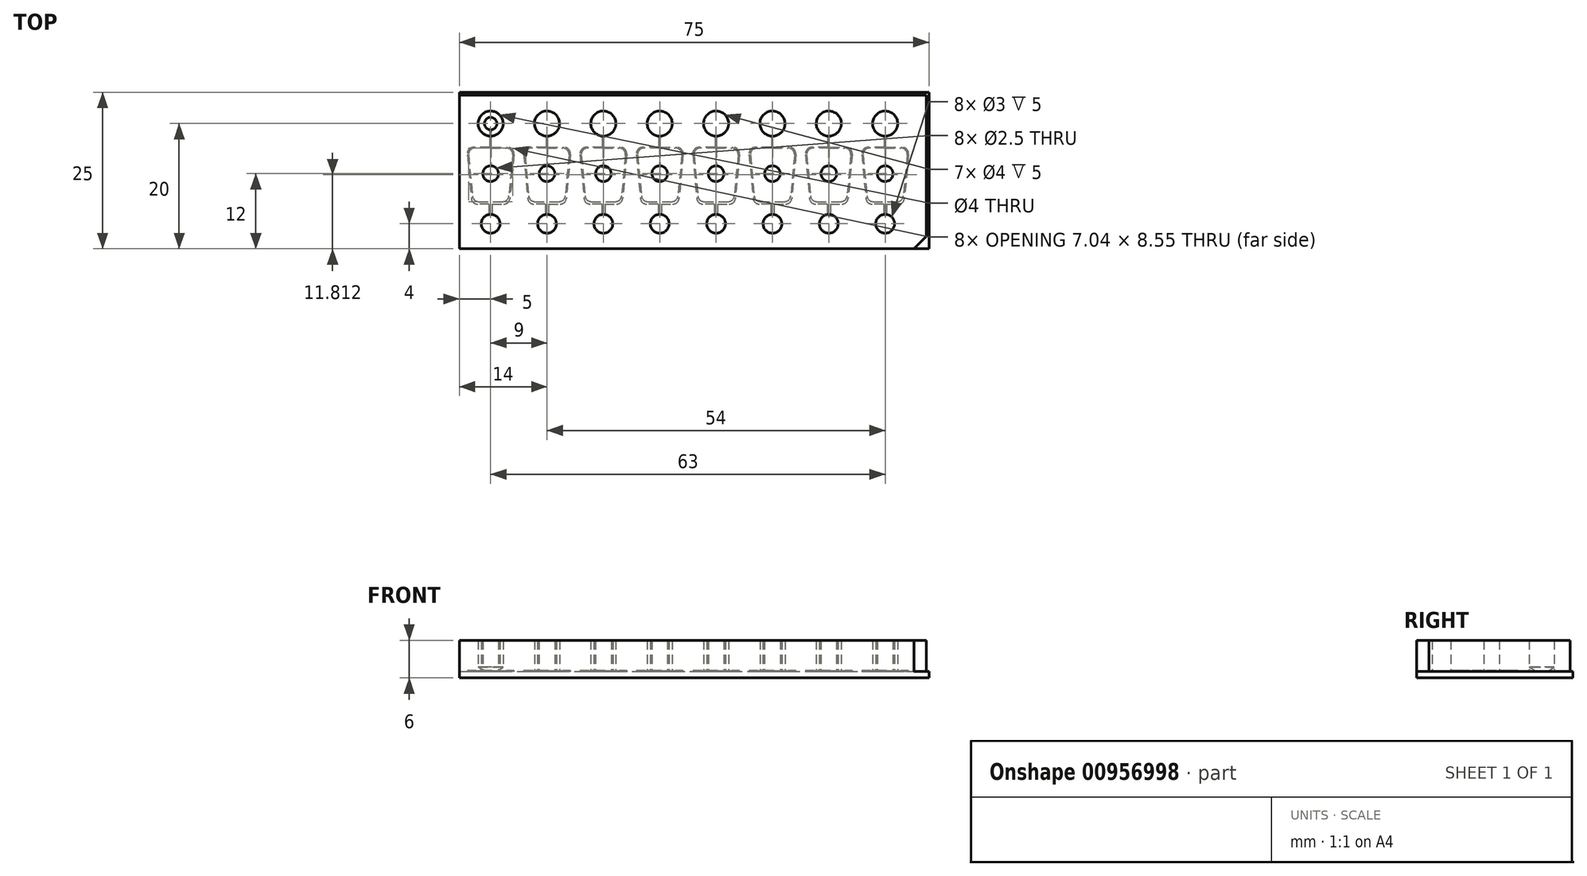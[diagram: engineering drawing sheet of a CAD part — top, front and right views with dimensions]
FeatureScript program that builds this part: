
annotation { "Feature Type Name" : "Feature", "Feature Type Description" : "" }
export const myFeature = defineFeature(function(context is Context, id is Id, definition is map)
    precondition{}
    {
        {
            assignVariable(context, id + "F0", {"name" : "offset_x_ports", "anyValue" : 5});
        }
        {
            var Q0;
            Q0=qCreatedBy(makeId("Top.planeOp"),FACE);
            var sketch = newSketch(context, id + "F1", { "sketchPlane" : qUnion([Q0])});
            skLineSegment(sketch, "E0.bottom", {"start": v(0, 0) * mm, "end": v(74.58, 0) * mm});
            skLineSegment(sketch, "E0.top", {"start": v(0, 24.53) * mm, "end": v(74.58, 24.53) * mm});
            skLineSegment(sketch, "E0.left", {"start": v(0, 0) * mm, "end": v(0, 24.53) * mm});
            skLineSegment(sketch, "E0.right", {"start": v(74.58, 0) * mm, "end": v(74.58, 24.53) * mm});
            skSolve(sketch);
        }
        {
            var Q0;
            Q0 = qSketchRegion(id + "F1", true);
            extrude(context, id + "F2", {"entities" : qUnion([Q0]), "depth" : 5 * mm, "offsetDistance" : 25 * mm});
        }
        {
            var Q0;
            Q0=qCreatedBy(makeId("Top.planeOp"),FACE);
            var sketch = newSketch(context, id + "F3", { "sketchPlane" : qUnion([Q0])});
            skCircle(sketch, "E1", {"center": v(5, 4) * mm, "radius": 1.5 * mm});
            skCircle(sketch, "E2", {"center": v(5, 20) * mm, "radius": 2 * mm});
            skCircle(sketch, "E3", {"center": v(5, 12) * mm, "radius": 1.25 * mm});
            skCircle(sketch, "E4.1.0.0", {"center": v(14, 4) * mm, "radius": 1.5 * mm});
            skCircle(sketch, "E4.1.0.1", {"center": v(14, 12) * mm, "radius": 1.25 * mm});
            skCircle(sketch, "E4.1.0.2", {"center": v(14, 20) * mm, "radius": 2 * mm});
            skCircle(sketch, "E4.2.0.0", {"center": v(23, 4) * mm, "radius": 1.5 * mm});
            skCircle(sketch, "E4.2.0.1", {"center": v(23, 12) * mm, "radius": 1.25 * mm});
            skCircle(sketch, "E4.2.0.2", {"center": v(23, 20) * mm, "radius": 2 * mm});
            skCircle(sketch, "E4.3.0.0", {"center": v(32, 4) * mm, "radius": 1.5 * mm});
            skCircle(sketch, "E4.3.0.1", {"center": v(32, 12) * mm, "radius": 1.25 * mm});
            skCircle(sketch, "E4.3.0.2", {"center": v(32, 20) * mm, "radius": 2 * mm});
            skCircle(sketch, "E4.4.0.0", {"center": v(41, 4) * mm, "radius": 1.5 * mm});
            skCircle(sketch, "E4.4.0.1", {"center": v(41, 12) * mm, "radius": 1.25 * mm});
            skCircle(sketch, "E4.4.0.2", {"center": v(41, 20) * mm, "radius": 2 * mm});
            skCircle(sketch, "E4.5.0.0", {"center": v(50, 4) * mm, "radius": 1.5 * mm});
            skCircle(sketch, "E4.5.0.1", {"center": v(50, 12) * mm, "radius": 1.25 * mm});
            skCircle(sketch, "E4.5.0.2", {"center": v(50, 20) * mm, "radius": 2 * mm});
            skCircle(sketch, "E4.6.0.0", {"center": v(59, 4) * mm, "radius": 1.5 * mm});
            skCircle(sketch, "E4.6.0.1", {"center": v(59, 12) * mm, "radius": 1.25 * mm});
            skCircle(sketch, "E4.6.0.2", {"center": v(59, 20) * mm, "radius": 2 * mm});
            skCircle(sketch, "E4.7.0.0", {"center": v(68, 4) * mm, "radius": 1.5 * mm});
            skCircle(sketch, "E4.7.0.1", {"center": v(68, 12) * mm, "radius": 1.25 * mm});
            skCircle(sketch, "E4.7.0.2", {"center": v(68, 20) * mm, "radius": 2 * mm});
            skLineSegment(sketch, "E4.direction1", {"start": v(5, 4) * mm, "end": v(14, 4) * mm, "construction": true});
            skSolve(sketch);
        }
        {
            var Q0;
            Q0 = qSketchRegion(id + "F3", true);
            var Q1;
            Q1=makeQuery(id+"F2.opExtrude","CAP_FACE",FACE,{"disambiguationData":[OSD([sQuery(id+"F1.wireOp",EDGE,"E0.bottom"),sQuery(id+"F1.wireOp",EDGE,"E0.top"),sQuery(id+"F1.wireOp",EDGE,"E0.left"),sQuery(id+"F1.wireOp",EDGE,"E0.right")])],"isStart":false});
            extrude(context, id + "F4", {"entities" : qUnion([Q0]), "operationType" : NewBodyOperationType.REMOVE, "endBound" : BoundingType.UP_TO_SURFACE, "depth" : 25 * mm, "endBoundEntityFace" : qUnion([Q1]), "offsetDistance" : 25 * mm});
        }
        {
            var Q0;
            Q0=makeQuery(id+"F2.opExtrude","SWEPT_EDGE",EDGE,{"disambiguationData":[OSD([sQuery(id+"F1.wireOp",EDGE,"E0.bottom"),sQuery(id+"F1.wireOp",EDGE,"E0.right")])]});
            chamfer(context, id + "F5", {"entities" : qUnion([Q0]), "width" : 2 * mm, "tangentPropagation" : true});
        }
        {
            var Q0;
            Q0=qCreatedBy(makeId("Top.planeOp"),FACE);
            var sketch = newSketch(context, id + "F6", { "sketchPlane" : qUnion([Q0])});
            skLineSegment(sketch, "E5.bottom", {"start": v(0, 0) * mm, "end": v(75, 0) * mm});
            skLineSegment(sketch, "E5.top", {"start": v(0, 25) * mm, "end": v(75, 25) * mm});
            skLineSegment(sketch, "E5.left", {"start": v(0, 0) * mm, "end": v(0, 25) * mm});
            skLineSegment(sketch, "E5.right", {"start": v(75, 0) * mm, "end": v(75, 25) * mm});
            skSolve(sketch);
        }
        {
            var Q0;
            Q0 = qSketchRegion(id + "F6", true);
            extrude(context, id + "F7", {"entities" : qUnion([Q0]), "oppositeDirection" : true, "depth" : 1 * mm, "offsetDistance" : 25 * mm});
        }
        {
            var Q0;
            Q0=qCreatedBy(makeId("Top.planeOp"),FACE);
            var sketch = newSketch(context, id + "F8", { "sketchPlane" : qUnion([Q0])});
            skPoint(sketch, "E6", {"position": v(5, 4) * mm});
            skLineSegment(sketch, "E7", {"start": v(5, 4) * mm, "end": v(5, 28.43) * mm});
            skSolve(sketch);
        }
        {
            var Q0;
            Q0=qCreatedBy(makeId("Right.planeOp"),FACE);
            cPlane(context, id + "F9", {"entities" : qUnion([Q0]), "cplaneType" : CPlaneType.OFFSET, "offset" : (getVariable(context, 'offset_x_ports')) * mm, "width" : 150 * mm, "height" : 150 * mm});
        }
        {
            var Q0;
            Q0=qCreatedBy(id+"F9.planeOp",FACE);
            var sketch = newSketch(context, id + "F10", { "sketchPlane" : qUnion([Q0])});
            skLineSegment(sketch, "E8", {"start": v(22, 4.38) * mm, "end": v(18, 4.38) * mm});
            skPoint(sketch, "E9", {"position": v(20, 4.38) * mm});
            skLineSegment(sketch, "E10", {"start": v(20, 4.38) * mm, "end": v(20, 0) * mm});
            skLineSegment(sketch, "E11", {"start": v(20, 0) * mm, "end": v(20, -2.07) * mm});
            skLineSegment(sketch, "E12", {"start": v(13.25, 0.89) * mm, "end": v(10.75, 0.89) * mm});
            skSolve(sketch);
        }
        {
            var Q0;
            Q0=qCreatedBy(id+"F9.planeOp",FACE);
            var sketch = newSketch(context, id + "F11", { "sketchPlane" : qUnion([Q0])});
            skLineSegment(sketch, "E13", {"start": v(22, 0) * mm, "end": v(22, 0.72) * mm});
            skLineSegment(sketch, "E14", {"start": v(22, 0.72) * mm, "end": v(21, 0) * mm});
            skLineSegment(sketch, "E15", {"start": v(21, 0) * mm, "end": v(22, 0) * mm});
            skSolve(sketch);
        }
        {
            var Q0;
            Q0 = qSketchRegion(id + "F11", true);
            var Q1;
            Q1=sQuery(id+"F10.wireOp",EDGE,"E10");
            revolve(context, id + "F12", {"operationType" : NewBodyOperationType.ADD, "surfaceOperationType" : NewSurfaceOperationType.NEW, "entities" : qUnion([Q0]), "axis" : qUnion([Q1]), "revolveType" : RevolveType.FULL});
        }
        {
            var Q0;
            Q0=qCreatedBy(makeId("Top.planeOp"),FACE);
            var sketch = newSketch(context, id + "F13", { "sketchPlane" : qUnion([Q0])});
            skLineSegment(sketch, "E16", {"start": v(5.03, 16.09) * mm, "end": v(7.52, 16.09) * mm});
            skLineSegment(sketch, "E17", {"start": v(5.2, 16.19) * mm, "end": v(7.73, 16.19) * mm});
            skLineSegment(sketch, "E18", {"start": v(5.25, 7.14) * mm, "end": v(5.25, 4) * mm});
            skPoint(sketch, "E19", {"position": v(5, 7.54) * mm});
            skLineSegment(sketch, "E20", {"start": v(5, 7.54) * mm, "end": v(6.92, 7.54) * mm});
            skPoint(sketch, "E21", {"position": v(5, 20) * mm});
            skPoint(sketch, "E22", {"position": v(5, 12) * mm});
            skLineSegment(sketch, "E23", {"start": v(5, 12) * mm, "end": v(5.03, 12) * mm});
            skLineSegment(sketch, "E24.trimOffspring", {"start": v(5.03, 16.09) * mm, "end": v(5.03, 12) * mm});
            skLineSegment(sketch, "E25", {"start": v(5.1, 16.29) * mm, "end": v(5.1, 20) * mm});
            skLineSegment(sketch, "E26", {"start": v(5, 20) * mm, "end": v(5.1, 20) * mm});
            skArc(sketch, "E27", {"start": v(5.1, 16.29) * mm, "mid": v(5.12, 16.22) * mm, "end": v(5.2, 16.19) * mm});
            skLineSegment(sketch, "E28", {"start": v(5.25, 7.14) * mm, "end": v(7.09, 7.14) * mm});
            skLineSegment(sketch, "E29", {"start": v(8.52, 15) * mm, "end": v(7.92, 8.44) * mm});
            skLineSegment(sketch, "E30", {"start": v(8.73, 15.1) * mm, "end": v(8.08, 8.04) * mm});
            skPoint(sketch, "E31.visualSharp", {"position": v(8, 7.14) * mm});
            skArc(sketch, "E31.filletArc", {"start": v(7.09, 7.14) * mm, "mid": v(7.76, 7.4) * mm, "end": v(8.08, 8.04) * mm});
            skPoint(sketch, "E32.visualSharp", {"position": v(7.83, 7.54) * mm});
            skArc(sketch, "E32.filletArc", {"start": v(6.92, 7.54) * mm, "mid": v(7.6, 7.8) * mm, "end": v(7.92, 8.44) * mm});
            skPoint(sketch, "E33.visualSharp", {"position": v(8.83, 16.19) * mm});
            skArc(sketch, "E33.filletArc", {"start": v(8.73, 15.1) * mm, "mid": v(8.47, 15.86) * mm, "end": v(7.73, 16.19) * mm});
            skPoint(sketch, "E34.visualSharp", {"position": v(8.62, 16.09) * mm});
            skArc(sketch, "E34.filletArc", {"start": v(8.52, 15) * mm, "mid": v(8.26, 15.76) * mm, "end": v(7.52, 16.09) * mm});
            skPoint(sketch, "E35", {"position": v(5, 4) * mm});
            skLineSegment(sketch, "E36", {"start": v(5, 4) * mm, "end": v(5.25, 4) * mm});
            skLineSegment(sketch, "E37.MirrorCS", {"start": v(5, 20) * mm, "end": v(4.91, 20) * mm});
            skLineSegment(sketch, "E38.MirrorCS", {"start": v(4.91, 16.29) * mm, "end": v(4.91, 20) * mm});
            skArc(sketch, "E39.MirrorCS", {"start": v(4.91, 16.29) * mm, "mid": v(4.88, 16.22) * mm, "end": v(4.8, 16.19) * mm});
            skLineSegment(sketch, "E40.MirrorCS", {"start": v(4.81, 16.19) * mm, "end": v(2.27, 16.19) * mm});
            skArc(sketch, "E41.MirrorCS", {"start": v(1.27, 15.1) * mm, "mid": v(1.53, 15.86) * mm, "end": v(2.27, 16.19) * mm});
            skArc(sketch, "E42.MirrorCS", {"start": v(1.48, 15) * mm, "mid": v(1.74, 15.76) * mm, "end": v(2.48, 16.09) * mm});
            skLineSegment(sketch, "E43.MirrorCS", {"start": v(4.98, 16.09) * mm, "end": v(2.48, 16.09) * mm});
            skLineSegment(sketch, "E44.MirrorCS", {"start": v(4.98, 16.09) * mm, "end": v(4.98, 12) * mm});
            skLineSegment(sketch, "E45.MirrorCS", {"start": v(1.48, 15) * mm, "end": v(2.08, 8.44) * mm});
            skLineSegment(sketch, "E46.MirrorCS", {"start": v(1.27, 15.1) * mm, "end": v(1.92, 8.04) * mm});
            skLineSegment(sketch, "E47.MirrorCS", {"start": v(5, 12) * mm, "end": v(4.98, 12) * mm});
            skArc(sketch, "E48.MirrorCS", {"start": v(3.08, 7.54) * mm, "mid": v(2.4, 7.8) * mm, "end": v(2.08, 8.44) * mm});
            skLineSegment(sketch, "E49.MirrorCS", {"start": v(5, 7.54) * mm, "end": v(3.08, 7.54) * mm});
            skLineSegment(sketch, "E50.MirrorCS", {"start": v(4.75, 7.14) * mm, "end": v(2.91, 7.14) * mm});
            skLineSegment(sketch, "E51.MirrorCS", {"start": v(4.75, 7.14) * mm, "end": v(4.75, 4) * mm});
            skLineSegment(sketch, "E52.MirrorCS", {"start": v(5, 4) * mm, "end": v(4.75, 4) * mm});
            skArc(sketch, "E53.MirrorCS", {"start": v(2.91, 7.14) * mm, "mid": v(2.24, 7.4) * mm, "end": v(1.92, 8.04) * mm});
            skPoint(sketch, "E54.1.0.0", {"position": v(14, 20) * mm});
            skLineSegment(sketch, "E54.1.0.1", {"start": v(14.1, 16.29) * mm, "end": v(14.1, 20) * mm});
            skLineSegment(sketch, "E54.1.0.2", {"start": v(14, 7.54) * mm, "end": v(15.92, 7.54) * mm});
            skLineSegment(sketch, "E54.1.0.3", {"start": v(13.98, 16.09) * mm, "end": v(13.98, 12) * mm});
            skPoint(sketch, "E54.1.0.4", {"position": v(16.83, 7.54) * mm});
            skLineSegment(sketch, "E54.1.0.5", {"start": v(14.25, 7.14) * mm, "end": v(14.25, 4) * mm});
            skLineSegment(sketch, "E54.1.0.6", {"start": v(10.27, 15.1) * mm, "end": v(10.92, 8.04) * mm});
            skPoint(sketch, "E54.1.0.7", {"position": v(14, 7.54) * mm});
            skPoint(sketch, "E54.1.0.8", {"position": v(17, 7.14) * mm});
            skPoint(sketch, "E54.1.0.9", {"position": v(17.83, 16.19) * mm});
            skPoint(sketch, "E54.1.0.10", {"position": v(14, 12) * mm});
            skPoint(sketch, "E54.1.0.11", {"position": v(14, 4) * mm});
            skLineSegment(sketch, "E54.1.0.12", {"start": v(13.91, 16.29) * mm, "end": v(13.91, 20) * mm});
            skLineSegment(sketch, "E54.1.0.13", {"start": v(13.75, 7.14) * mm, "end": v(13.75, 4) * mm});
            skPoint(sketch, "E54.1.0.14", {"position": v(17.62, 16.09) * mm});
            skLineSegment(sketch, "E54.1.0.15", {"start": v(14.03, 16.09) * mm, "end": v(14.03, 12) * mm});
            skLineSegment(sketch, "E54.1.0.16", {"start": v(10.48, 15) * mm, "end": v(11.08, 8.44) * mm});
            skLineSegment(sketch, "E54.1.0.17", {"start": v(13.8, 16.19) * mm, "end": v(11.27, 16.19) * mm});
            skLineSegment(sketch, "E54.1.0.18", {"start": v(17.73, 15.1) * mm, "end": v(17.08, 8.04) * mm});
            skArc(sketch, "E54.1.0.19", {"start": v(10.27, 15.1) * mm, "mid": v(10.53, 15.86) * mm, "end": v(11.27, 16.19) * mm});
            skLineSegment(sketch, "E54.1.0.20", {"start": v(17.52, 15) * mm, "end": v(16.92, 8.44) * mm});
            skArc(sketch, "E54.1.0.21", {"start": v(17.73, 15.1) * mm, "mid": v(17.47, 15.86) * mm, "end": v(16.73, 16.19) * mm});
            skLineSegment(sketch, "E54.1.0.22", {"start": v(14.2, 16.19) * mm, "end": v(16.73, 16.19) * mm});
            skLineSegment(sketch, "E54.1.0.23", {"start": v(13.98, 16.09) * mm, "end": v(11.48, 16.09) * mm});
            skLineSegment(sketch, "E54.1.0.24", {"start": v(14.25, 7.14) * mm, "end": v(16.09, 7.14) * mm});
            skArc(sketch, "E54.1.0.25", {"start": v(12.08, 7.54) * mm, "mid": v(11.4, 7.8) * mm, "end": v(11.08, 8.44) * mm});
            skArc(sketch, "E54.1.0.26", {"start": v(16.09, 7.14) * mm, "mid": v(16.76, 7.4) * mm, "end": v(17.08, 8.04) * mm});
            skArc(sketch, "E54.1.0.27", {"start": v(10.48, 15) * mm, "mid": v(10.74, 15.76) * mm, "end": v(11.48, 16.09) * mm});
            skLineSegment(sketch, "E54.1.0.28", {"start": v(14, 7.54) * mm, "end": v(12.08, 7.54) * mm});
            skArc(sketch, "E54.1.0.29", {"start": v(17.52, 15) * mm, "mid": v(17.26, 15.76) * mm, "end": v(16.52, 16.09) * mm});
            skArc(sketch, "E54.1.0.30", {"start": v(15.92, 7.54) * mm, "mid": v(16.6, 7.8) * mm, "end": v(16.92, 8.44) * mm});
            skLineSegment(sketch, "E54.1.0.31", {"start": v(14.03, 16.09) * mm, "end": v(16.52, 16.09) * mm});
            skArc(sketch, "E54.1.0.32", {"start": v(11.91, 7.14) * mm, "mid": v(11.24, 7.4) * mm, "end": v(10.92, 8.04) * mm});
            skLineSegment(sketch, "E54.1.0.33", {"start": v(13.75, 7.14) * mm, "end": v(11.91, 7.14) * mm});
            skLineSegment(sketch, "E54.1.0.34", {"start": v(14, 4) * mm, "end": v(13.75, 4) * mm});
            skLineSegment(sketch, "E54.1.0.35", {"start": v(14, 20) * mm, "end": v(13.91, 20) * mm});
            skLineSegment(sketch, "E54.1.0.36", {"start": v(14, 4) * mm, "end": v(14.25, 4) * mm});
            skLineSegment(sketch, "E54.1.0.37", {"start": v(14, 12) * mm, "end": v(13.98, 12) * mm});
            skLineSegment(sketch, "E54.1.0.38", {"start": v(14, 12) * mm, "end": v(14.03, 12) * mm});
            skLineSegment(sketch, "E54.1.0.39", {"start": v(14, 20) * mm, "end": v(14.1, 20) * mm});
            skArc(sketch, "E54.1.0.40", {"start": v(14.1, 16.29) * mm, "mid": v(14.12, 16.22) * mm, "end": v(14.2, 16.19) * mm});
            skArc(sketch, "E54.1.0.41", {"start": v(13.91, 16.29) * mm, "mid": v(13.88, 16.22) * mm, "end": v(13.8, 16.19) * mm});
            skPoint(sketch, "E54.2.0.0", {"position": v(23, 20) * mm});
            skLineSegment(sketch, "E54.2.0.1", {"start": v(23.1, 16.29) * mm, "end": v(23.1, 20) * mm});
            skLineSegment(sketch, "E54.2.0.2", {"start": v(23, 7.54) * mm, "end": v(24.92, 7.54) * mm});
            skLineSegment(sketch, "E54.2.0.3", {"start": v(22.98, 16.09) * mm, "end": v(22.98, 12) * mm});
            skPoint(sketch, "E54.2.0.4", {"position": v(25.83, 7.54) * mm});
            skLineSegment(sketch, "E54.2.0.5", {"start": v(23.25, 7.14) * mm, "end": v(23.25, 4) * mm});
            skLineSegment(sketch, "E54.2.0.6", {"start": v(19.27, 15.1) * mm, "end": v(19.92, 8.04) * mm});
            skPoint(sketch, "E54.2.0.7", {"position": v(23, 7.54) * mm});
            skPoint(sketch, "E54.2.0.8", {"position": v(26, 7.14) * mm});
            skPoint(sketch, "E54.2.0.9", {"position": v(26.83, 16.19) * mm});
            skPoint(sketch, "E54.2.0.10", {"position": v(23, 12) * mm});
            skPoint(sketch, "E54.2.0.11", {"position": v(23, 4) * mm});
            skLineSegment(sketch, "E54.2.0.12", {"start": v(22.91, 16.29) * mm, "end": v(22.91, 20) * mm});
            skLineSegment(sketch, "E54.2.0.13", {"start": v(22.75, 7.14) * mm, "end": v(22.75, 4) * mm});
            skPoint(sketch, "E54.2.0.14", {"position": v(26.62, 16.09) * mm});
            skLineSegment(sketch, "E54.2.0.15", {"start": v(23.03, 16.09) * mm, "end": v(23.03, 12) * mm});
            skLineSegment(sketch, "E54.2.0.16", {"start": v(19.48, 15) * mm, "end": v(20.08, 8.44) * mm});
            skLineSegment(sketch, "E54.2.0.17", {"start": v(22.81, 16.19) * mm, "end": v(20.27, 16.19) * mm});
            skLineSegment(sketch, "E54.2.0.18", {"start": v(26.73, 15.1) * mm, "end": v(26.08, 8.04) * mm});
            skArc(sketch, "E54.2.0.19", {"start": v(19.27, 15.1) * mm, "mid": v(19.53, 15.86) * mm, "end": v(20.27, 16.19) * mm});
            skLineSegment(sketch, "E54.2.0.20", {"start": v(26.52, 15) * mm, "end": v(25.92, 8.44) * mm});
            skArc(sketch, "E54.2.0.21", {"start": v(26.73, 15.1) * mm, "mid": v(26.47, 15.86) * mm, "end": v(25.73, 16.19) * mm});
            skLineSegment(sketch, "E54.2.0.22", {"start": v(23.2, 16.19) * mm, "end": v(25.73, 16.19) * mm});
            skLineSegment(sketch, "E54.2.0.23", {"start": v(22.98, 16.09) * mm, "end": v(20.48, 16.09) * mm});
            skLineSegment(sketch, "E54.2.0.24", {"start": v(23.25, 7.14) * mm, "end": v(25.09, 7.14) * mm});
            skArc(sketch, "E54.2.0.25", {"start": v(21.08, 7.54) * mm, "mid": v(20.4, 7.8) * mm, "end": v(20.08, 8.44) * mm});
            skArc(sketch, "E54.2.0.26", {"start": v(25.09, 7.14) * mm, "mid": v(25.76, 7.4) * mm, "end": v(26.08, 8.04) * mm});
            skArc(sketch, "E54.2.0.27", {"start": v(19.48, 15) * mm, "mid": v(19.74, 15.76) * mm, "end": v(20.48, 16.09) * mm});
            skLineSegment(sketch, "E54.2.0.28", {"start": v(23, 7.54) * mm, "end": v(21.08, 7.54) * mm});
            skArc(sketch, "E54.2.0.29", {"start": v(26.52, 15) * mm, "mid": v(26.26, 15.76) * mm, "end": v(25.52, 16.09) * mm});
            skArc(sketch, "E54.2.0.30", {"start": v(24.92, 7.54) * mm, "mid": v(25.6, 7.8) * mm, "end": v(25.92, 8.44) * mm});
            skLineSegment(sketch, "E54.2.0.31", {"start": v(23.03, 16.09) * mm, "end": v(25.52, 16.09) * mm});
            skArc(sketch, "E54.2.0.32", {"start": v(20.91, 7.14) * mm, "mid": v(20.24, 7.4) * mm, "end": v(19.92, 8.04) * mm});
            skLineSegment(sketch, "E54.2.0.33", {"start": v(22.75, 7.14) * mm, "end": v(20.91, 7.14) * mm});
            skLineSegment(sketch, "E54.2.0.34", {"start": v(23, 4) * mm, "end": v(22.75, 4) * mm});
            skLineSegment(sketch, "E54.2.0.35", {"start": v(23, 20) * mm, "end": v(22.91, 20) * mm});
            skLineSegment(sketch, "E54.2.0.36", {"start": v(23, 4) * mm, "end": v(23.25, 4) * mm});
            skLineSegment(sketch, "E54.2.0.37", {"start": v(23, 12) * mm, "end": v(22.98, 12) * mm});
            skLineSegment(sketch, "E54.2.0.38", {"start": v(23, 12) * mm, "end": v(23.03, 12) * mm});
            skLineSegment(sketch, "E54.2.0.39", {"start": v(23, 20) * mm, "end": v(23.1, 20) * mm});
            skArc(sketch, "E54.2.0.40", {"start": v(23.1, 16.29) * mm, "mid": v(23.12, 16.22) * mm, "end": v(23.2, 16.19) * mm});
            skArc(sketch, "E54.2.0.41", {"start": v(22.91, 16.29) * mm, "mid": v(22.88, 16.22) * mm, "end": v(22.8, 16.19) * mm});
            skPoint(sketch, "E54.3.0.0", {"position": v(32, 20) * mm});
            skLineSegment(sketch, "E54.3.0.1", {"start": v(32.1, 16.29) * mm, "end": v(32.1, 20) * mm});
            skLineSegment(sketch, "E54.3.0.2", {"start": v(32, 7.54) * mm, "end": v(33.92, 7.54) * mm});
            skLineSegment(sketch, "E54.3.0.3", {"start": v(31.98, 16.09) * mm, "end": v(31.98, 12) * mm});
            skPoint(sketch, "E54.3.0.4", {"position": v(34.83, 7.54) * mm});
            skLineSegment(sketch, "E54.3.0.5", {"start": v(32.25, 7.14) * mm, "end": v(32.25, 4) * mm});
            skLineSegment(sketch, "E54.3.0.6", {"start": v(28.27, 15.1) * mm, "end": v(28.92, 8.04) * mm});
            skPoint(sketch, "E54.3.0.7", {"position": v(32, 7.54) * mm});
            skPoint(sketch, "E54.3.0.8", {"position": v(35, 7.14) * mm});
            skPoint(sketch, "E54.3.0.9", {"position": v(35.83, 16.19) * mm});
            skPoint(sketch, "E54.3.0.10", {"position": v(32, 12) * mm});
            skPoint(sketch, "E54.3.0.11", {"position": v(32, 4) * mm});
            skLineSegment(sketch, "E54.3.0.12", {"start": v(31.91, 16.29) * mm, "end": v(31.91, 20) * mm});
            skLineSegment(sketch, "E54.3.0.13", {"start": v(31.75, 7.14) * mm, "end": v(31.75, 4) * mm});
            skPoint(sketch, "E54.3.0.14", {"position": v(35.62, 16.09) * mm});
            skLineSegment(sketch, "E54.3.0.15", {"start": v(32.03, 16.09) * mm, "end": v(32.03, 12) * mm});
            skLineSegment(sketch, "E54.3.0.16", {"start": v(28.48, 15) * mm, "end": v(29.08, 8.44) * mm});
            skLineSegment(sketch, "E54.3.0.17", {"start": v(31.81, 16.19) * mm, "end": v(29.27, 16.19) * mm});
            skLineSegment(sketch, "E54.3.0.18", {"start": v(35.73, 15.1) * mm, "end": v(35.08, 8.04) * mm});
            skArc(sketch, "E54.3.0.19", {"start": v(28.27, 15.1) * mm, "mid": v(28.53, 15.86) * mm, "end": v(29.27, 16.19) * mm});
            skLineSegment(sketch, "E54.3.0.20", {"start": v(35.52, 15) * mm, "end": v(34.92, 8.44) * mm});
            skArc(sketch, "E54.3.0.21", {"start": v(35.73, 15.1) * mm, "mid": v(35.47, 15.86) * mm, "end": v(34.73, 16.19) * mm});
            skLineSegment(sketch, "E54.3.0.22", {"start": v(32.2, 16.19) * mm, "end": v(34.73, 16.19) * mm});
            skLineSegment(sketch, "E54.3.0.23", {"start": v(31.98, 16.09) * mm, "end": v(29.48, 16.09) * mm});
            skLineSegment(sketch, "E54.3.0.24", {"start": v(32.25, 7.14) * mm, "end": v(34.09, 7.14) * mm});
            skArc(sketch, "E54.3.0.25", {"start": v(30.08, 7.54) * mm, "mid": v(29.4, 7.8) * mm, "end": v(29.08, 8.44) * mm});
            skArc(sketch, "E54.3.0.26", {"start": v(34.09, 7.14) * mm, "mid": v(34.76, 7.4) * mm, "end": v(35.08, 8.04) * mm});
            skArc(sketch, "E54.3.0.27", {"start": v(28.48, 15) * mm, "mid": v(28.74, 15.76) * mm, "end": v(29.48, 16.09) * mm});
            skLineSegment(sketch, "E54.3.0.28", {"start": v(32, 7.54) * mm, "end": v(30.08, 7.54) * mm});
            skArc(sketch, "E54.3.0.29", {"start": v(35.52, 15) * mm, "mid": v(35.26, 15.76) * mm, "end": v(34.52, 16.09) * mm});
            skArc(sketch, "E54.3.0.30", {"start": v(33.92, 7.54) * mm, "mid": v(34.6, 7.8) * mm, "end": v(34.92, 8.44) * mm});
            skLineSegment(sketch, "E54.3.0.31", {"start": v(32.03, 16.09) * mm, "end": v(34.52, 16.09) * mm});
            skArc(sketch, "E54.3.0.32", {"start": v(29.91, 7.14) * mm, "mid": v(29.24, 7.4) * mm, "end": v(28.92, 8.04) * mm});
            skLineSegment(sketch, "E54.3.0.33", {"start": v(31.75, 7.14) * mm, "end": v(29.91, 7.14) * mm});
            skLineSegment(sketch, "E54.3.0.34", {"start": v(32, 4) * mm, "end": v(31.75, 4) * mm});
            skLineSegment(sketch, "E54.3.0.35", {"start": v(32, 20) * mm, "end": v(31.91, 20) * mm});
            skLineSegment(sketch, "E54.3.0.36", {"start": v(32, 4) * mm, "end": v(32.25, 4) * mm});
            skLineSegment(sketch, "E54.3.0.37", {"start": v(32, 12) * mm, "end": v(31.98, 12) * mm});
            skLineSegment(sketch, "E54.3.0.38", {"start": v(32, 12) * mm, "end": v(32.03, 12) * mm});
            skLineSegment(sketch, "E54.3.0.39", {"start": v(32, 20) * mm, "end": v(32.1, 20) * mm});
            skArc(sketch, "E54.3.0.40", {"start": v(32.1, 16.29) * mm, "mid": v(32.12, 16.22) * mm, "end": v(32.2, 16.19) * mm});
            skArc(sketch, "E54.3.0.41", {"start": v(31.91, 16.29) * mm, "mid": v(31.88, 16.22) * mm, "end": v(31.8, 16.19) * mm});
            skPoint(sketch, "E54.4.0.0", {"position": v(41, 20) * mm});
            skLineSegment(sketch, "E54.4.0.1", {"start": v(41.1, 16.29) * mm, "end": v(41.1, 20) * mm});
            skLineSegment(sketch, "E54.4.0.2", {"start": v(41, 7.54) * mm, "end": v(42.92, 7.54) * mm});
            skLineSegment(sketch, "E54.4.0.3", {"start": v(40.98, 16.09) * mm, "end": v(40.98, 12) * mm});
            skPoint(sketch, "E54.4.0.4", {"position": v(43.83, 7.54) * mm});
            skLineSegment(sketch, "E54.4.0.5", {"start": v(41.25, 7.14) * mm, "end": v(41.25, 4) * mm});
            skLineSegment(sketch, "E54.4.0.6", {"start": v(37.27, 15.1) * mm, "end": v(37.92, 8.04) * mm});
            skPoint(sketch, "E54.4.0.7", {"position": v(41, 7.54) * mm});
            skPoint(sketch, "E54.4.0.8", {"position": v(44, 7.14) * mm});
            skPoint(sketch, "E54.4.0.9", {"position": v(44.83, 16.19) * mm});
            skPoint(sketch, "E54.4.0.10", {"position": v(41, 12) * mm});
            skPoint(sketch, "E54.4.0.11", {"position": v(41, 4) * mm});
            skLineSegment(sketch, "E54.4.0.12", {"start": v(40.91, 16.29) * mm, "end": v(40.91, 20) * mm});
            skLineSegment(sketch, "E54.4.0.13", {"start": v(40.75, 7.14) * mm, "end": v(40.75, 4) * mm});
            skPoint(sketch, "E54.4.0.14", {"position": v(44.62, 16.09) * mm});
            skLineSegment(sketch, "E54.4.0.15", {"start": v(41.03, 16.09) * mm, "end": v(41.03, 12) * mm});
            skLineSegment(sketch, "E54.4.0.16", {"start": v(37.48, 15) * mm, "end": v(38.08, 8.44) * mm});
            skLineSegment(sketch, "E54.4.0.17", {"start": v(40.81, 16.19) * mm, "end": v(38.27, 16.19) * mm});
            skLineSegment(sketch, "E54.4.0.18", {"start": v(44.73, 15.1) * mm, "end": v(44.08, 8.04) * mm});
            skArc(sketch, "E54.4.0.19", {"start": v(37.27, 15.1) * mm, "mid": v(37.53, 15.86) * mm, "end": v(38.27, 16.19) * mm});
            skLineSegment(sketch, "E54.4.0.20", {"start": v(44.52, 15) * mm, "end": v(43.92, 8.44) * mm});
            skArc(sketch, "E54.4.0.21", {"start": v(44.73, 15.1) * mm, "mid": v(44.47, 15.86) * mm, "end": v(43.73, 16.19) * mm});
            skLineSegment(sketch, "E54.4.0.22", {"start": v(41.2, 16.19) * mm, "end": v(43.73, 16.19) * mm});
            skLineSegment(sketch, "E54.4.0.23", {"start": v(40.98, 16.09) * mm, "end": v(38.48, 16.09) * mm});
            skLineSegment(sketch, "E54.4.0.24", {"start": v(41.25, 7.14) * mm, "end": v(43.09, 7.14) * mm});
            skArc(sketch, "E54.4.0.25", {"start": v(39.08, 7.54) * mm, "mid": v(38.4, 7.8) * mm, "end": v(38.08, 8.44) * mm});
            skArc(sketch, "E54.4.0.26", {"start": v(43.09, 7.14) * mm, "mid": v(43.76, 7.4) * mm, "end": v(44.08, 8.04) * mm});
            skArc(sketch, "E54.4.0.27", {"start": v(37.48, 15) * mm, "mid": v(37.74, 15.76) * mm, "end": v(38.48, 16.09) * mm});
            skLineSegment(sketch, "E54.4.0.28", {"start": v(41, 7.54) * mm, "end": v(39.08, 7.54) * mm});
            skArc(sketch, "E54.4.0.29", {"start": v(44.52, 15) * mm, "mid": v(44.26, 15.76) * mm, "end": v(43.52, 16.09) * mm});
            skArc(sketch, "E54.4.0.30", {"start": v(42.92, 7.54) * mm, "mid": v(43.6, 7.8) * mm, "end": v(43.92, 8.44) * mm});
            skLineSegment(sketch, "E54.4.0.31", {"start": v(41.03, 16.09) * mm, "end": v(43.52, 16.09) * mm});
            skArc(sketch, "E54.4.0.32", {"start": v(38.91, 7.14) * mm, "mid": v(38.24, 7.4) * mm, "end": v(37.92, 8.04) * mm});
            skLineSegment(sketch, "E54.4.0.33", {"start": v(40.75, 7.14) * mm, "end": v(38.91, 7.14) * mm});
            skLineSegment(sketch, "E54.4.0.34", {"start": v(41, 4) * mm, "end": v(40.75, 4) * mm});
            skLineSegment(sketch, "E54.4.0.35", {"start": v(41, 20) * mm, "end": v(40.91, 20) * mm});
            skLineSegment(sketch, "E54.4.0.36", {"start": v(41, 4) * mm, "end": v(41.25, 4) * mm});
            skLineSegment(sketch, "E54.4.0.37", {"start": v(41, 12) * mm, "end": v(40.98, 12) * mm});
            skLineSegment(sketch, "E54.4.0.38", {"start": v(41, 12) * mm, "end": v(41.03, 12) * mm});
            skLineSegment(sketch, "E54.4.0.39", {"start": v(41, 20) * mm, "end": v(41.1, 20) * mm});
            skArc(sketch, "E54.4.0.40", {"start": v(41.1, 16.29) * mm, "mid": v(41.12, 16.22) * mm, "end": v(41.2, 16.19) * mm});
            skArc(sketch, "E54.4.0.41", {"start": v(40.91, 16.29) * mm, "mid": v(40.88, 16.22) * mm, "end": v(40.8, 16.19) * mm});
            skPoint(sketch, "E54.5.0.0", {"position": v(50, 20) * mm});
            skLineSegment(sketch, "E54.5.0.1", {"start": v(50.1, 16.29) * mm, "end": v(50.1, 20) * mm});
            skLineSegment(sketch, "E54.5.0.2", {"start": v(50, 7.54) * mm, "end": v(51.92, 7.54) * mm});
            skLineSegment(sketch, "E54.5.0.3", {"start": v(49.98, 16.09) * mm, "end": v(49.98, 12) * mm});
            skPoint(sketch, "E54.5.0.4", {"position": v(52.83, 7.54) * mm});
            skLineSegment(sketch, "E54.5.0.5", {"start": v(50.25, 7.14) * mm, "end": v(50.25, 4) * mm});
            skLineSegment(sketch, "E54.5.0.6", {"start": v(46.27, 15.1) * mm, "end": v(46.92, 8.04) * mm});
            skPoint(sketch, "E54.5.0.7", {"position": v(50, 7.54) * mm});
            skPoint(sketch, "E54.5.0.8", {"position": v(53, 7.14) * mm});
            skPoint(sketch, "E54.5.0.9", {"position": v(53.83, 16.19) * mm});
            skPoint(sketch, "E54.5.0.10", {"position": v(50, 12) * mm});
            skPoint(sketch, "E54.5.0.11", {"position": v(50, 4) * mm});
            skLineSegment(sketch, "E54.5.0.12", {"start": v(49.91, 16.29) * mm, "end": v(49.91, 20) * mm});
            skLineSegment(sketch, "E54.5.0.13", {"start": v(49.75, 7.14) * mm, "end": v(49.75, 4) * mm});
            skPoint(sketch, "E54.5.0.14", {"position": v(53.62, 16.09) * mm});
            skLineSegment(sketch, "E54.5.0.15", {"start": v(50.03, 16.09) * mm, "end": v(50.03, 12) * mm});
            skLineSegment(sketch, "E54.5.0.16", {"start": v(46.48, 15) * mm, "end": v(47.08, 8.44) * mm});
            skLineSegment(sketch, "E54.5.0.17", {"start": v(49.81, 16.19) * mm, "end": v(47.27, 16.19) * mm});
            skLineSegment(sketch, "E54.5.0.18", {"start": v(53.73, 15.1) * mm, "end": v(53.08, 8.04) * mm});
            skArc(sketch, "E54.5.0.19", {"start": v(46.27, 15.1) * mm, "mid": v(46.53, 15.86) * mm, "end": v(47.27, 16.19) * mm});
            skLineSegment(sketch, "E54.5.0.20", {"start": v(53.52, 15) * mm, "end": v(52.92, 8.44) * mm});
            skArc(sketch, "E54.5.0.21", {"start": v(53.73, 15.1) * mm, "mid": v(53.47, 15.86) * mm, "end": v(52.73, 16.19) * mm});
            skLineSegment(sketch, "E54.5.0.22", {"start": v(50.2, 16.19) * mm, "end": v(52.73, 16.19) * mm});
            skLineSegment(sketch, "E54.5.0.23", {"start": v(49.98, 16.09) * mm, "end": v(47.48, 16.09) * mm});
            skLineSegment(sketch, "E54.5.0.24", {"start": v(50.25, 7.14) * mm, "end": v(52.09, 7.14) * mm});
            skArc(sketch, "E54.5.0.25", {"start": v(48.08, 7.54) * mm, "mid": v(47.4, 7.8) * mm, "end": v(47.08, 8.44) * mm});
            skArc(sketch, "E54.5.0.26", {"start": v(52.09, 7.14) * mm, "mid": v(52.76, 7.4) * mm, "end": v(53.08, 8.04) * mm});
            skArc(sketch, "E54.5.0.27", {"start": v(46.48, 15) * mm, "mid": v(46.74, 15.76) * mm, "end": v(47.48, 16.09) * mm});
            skLineSegment(sketch, "E54.5.0.28", {"start": v(50, 7.54) * mm, "end": v(48.08, 7.54) * mm});
            skArc(sketch, "E54.5.0.29", {"start": v(53.52, 15) * mm, "mid": v(53.26, 15.76) * mm, "end": v(52.52, 16.09) * mm});
            skArc(sketch, "E54.5.0.30", {"start": v(51.92, 7.54) * mm, "mid": v(52.6, 7.8) * mm, "end": v(52.92, 8.44) * mm});
            skLineSegment(sketch, "E54.5.0.31", {"start": v(50.03, 16.09) * mm, "end": v(52.52, 16.09) * mm});
            skArc(sketch, "E54.5.0.32", {"start": v(47.91, 7.14) * mm, "mid": v(47.24, 7.4) * mm, "end": v(46.92, 8.04) * mm});
            skLineSegment(sketch, "E54.5.0.33", {"start": v(49.75, 7.14) * mm, "end": v(47.91, 7.14) * mm});
            skLineSegment(sketch, "E54.5.0.34", {"start": v(50, 4) * mm, "end": v(49.75, 4) * mm});
            skLineSegment(sketch, "E54.5.0.35", {"start": v(50, 20) * mm, "end": v(49.91, 20) * mm});
            skLineSegment(sketch, "E54.5.0.36", {"start": v(50, 4) * mm, "end": v(50.25, 4) * mm});
            skLineSegment(sketch, "E54.5.0.37", {"start": v(50, 12) * mm, "end": v(49.98, 12) * mm});
            skLineSegment(sketch, "E54.5.0.38", {"start": v(50, 12) * mm, "end": v(50.03, 12) * mm});
            skLineSegment(sketch, "E54.5.0.39", {"start": v(50, 20) * mm, "end": v(50.1, 20) * mm});
            skArc(sketch, "E54.5.0.40", {"start": v(50.1, 16.29) * mm, "mid": v(50.12, 16.22) * mm, "end": v(50.2, 16.19) * mm});
            skArc(sketch, "E54.5.0.41", {"start": v(49.91, 16.29) * mm, "mid": v(49.88, 16.22) * mm, "end": v(49.8, 16.19) * mm});
            skPoint(sketch, "E54.6.0.0", {"position": v(59, 20) * mm});
            skLineSegment(sketch, "E54.6.0.1", {"start": v(59.1, 16.29) * mm, "end": v(59.1, 20) * mm});
            skLineSegment(sketch, "E54.6.0.2", {"start": v(59, 7.54) * mm, "end": v(60.92, 7.54) * mm});
            skLineSegment(sketch, "E54.6.0.3", {"start": v(58.98, 16.09) * mm, "end": v(58.98, 12) * mm});
            skPoint(sketch, "E54.6.0.4", {"position": v(61.83, 7.54) * mm});
            skLineSegment(sketch, "E54.6.0.5", {"start": v(59.25, 7.14) * mm, "end": v(59.25, 4) * mm});
            skLineSegment(sketch, "E54.6.0.6", {"start": v(55.27, 15.1) * mm, "end": v(55.92, 8.04) * mm});
            skPoint(sketch, "E54.6.0.7", {"position": v(59, 7.54) * mm});
            skPoint(sketch, "E54.6.0.8", {"position": v(62, 7.14) * mm});
            skPoint(sketch, "E54.6.0.9", {"position": v(62.83, 16.19) * mm});
            skPoint(sketch, "E54.6.0.10", {"position": v(59, 12) * mm});
            skPoint(sketch, "E54.6.0.11", {"position": v(59, 4) * mm});
            skLineSegment(sketch, "E54.6.0.12", {"start": v(58.91, 16.29) * mm, "end": v(58.91, 20) * mm});
            skLineSegment(sketch, "E54.6.0.13", {"start": v(58.75, 7.14) * mm, "end": v(58.75, 4) * mm});
            skPoint(sketch, "E54.6.0.14", {"position": v(62.62, 16.09) * mm});
            skLineSegment(sketch, "E54.6.0.15", {"start": v(59.03, 16.09) * mm, "end": v(59.03, 12) * mm});
            skLineSegment(sketch, "E54.6.0.16", {"start": v(55.48, 15) * mm, "end": v(56.08, 8.44) * mm});
            skLineSegment(sketch, "E54.6.0.17", {"start": v(58.81, 16.19) * mm, "end": v(56.27, 16.19) * mm});
            skLineSegment(sketch, "E54.6.0.18", {"start": v(62.73, 15.1) * mm, "end": v(62.08, 8.04) * mm});
            skArc(sketch, "E54.6.0.19", {"start": v(55.27, 15.1) * mm, "mid": v(55.53, 15.86) * mm, "end": v(56.27, 16.19) * mm});
            skLineSegment(sketch, "E54.6.0.20", {"start": v(62.52, 15) * mm, "end": v(61.92, 8.44) * mm});
            skArc(sketch, "E54.6.0.21", {"start": v(62.73, 15.1) * mm, "mid": v(62.47, 15.86) * mm, "end": v(61.73, 16.19) * mm});
            skLineSegment(sketch, "E54.6.0.22", {"start": v(59.2, 16.19) * mm, "end": v(61.73, 16.19) * mm});
            skLineSegment(sketch, "E54.6.0.23", {"start": v(58.98, 16.09) * mm, "end": v(56.48, 16.09) * mm});
            skLineSegment(sketch, "E54.6.0.24", {"start": v(59.25, 7.14) * mm, "end": v(61.09, 7.14) * mm});
            skArc(sketch, "E54.6.0.25", {"start": v(57.08, 7.54) * mm, "mid": v(56.4, 7.8) * mm, "end": v(56.08, 8.44) * mm});
            skArc(sketch, "E54.6.0.26", {"start": v(61.09, 7.14) * mm, "mid": v(61.76, 7.4) * mm, "end": v(62.08, 8.04) * mm});
            skArc(sketch, "E54.6.0.27", {"start": v(55.48, 15) * mm, "mid": v(55.74, 15.76) * mm, "end": v(56.48, 16.09) * mm});
            skLineSegment(sketch, "E54.6.0.28", {"start": v(59, 7.54) * mm, "end": v(57.08, 7.54) * mm});
            skArc(sketch, "E54.6.0.29", {"start": v(62.52, 15) * mm, "mid": v(62.26, 15.76) * mm, "end": v(61.52, 16.09) * mm});
            skArc(sketch, "E54.6.0.30", {"start": v(60.92, 7.54) * mm, "mid": v(61.6, 7.8) * mm, "end": v(61.92, 8.44) * mm});
            skLineSegment(sketch, "E54.6.0.31", {"start": v(59.03, 16.09) * mm, "end": v(61.52, 16.09) * mm});
            skArc(sketch, "E54.6.0.32", {"start": v(56.91, 7.14) * mm, "mid": v(56.24, 7.4) * mm, "end": v(55.92, 8.04) * mm});
            skLineSegment(sketch, "E54.6.0.33", {"start": v(58.75, 7.14) * mm, "end": v(56.91, 7.14) * mm});
            skLineSegment(sketch, "E54.6.0.34", {"start": v(59, 4) * mm, "end": v(58.75, 4) * mm});
            skLineSegment(sketch, "E54.6.0.35", {"start": v(59, 20) * mm, "end": v(58.91, 20) * mm});
            skLineSegment(sketch, "E54.6.0.36", {"start": v(59, 4) * mm, "end": v(59.25, 4) * mm});
            skLineSegment(sketch, "E54.6.0.37", {"start": v(59, 12) * mm, "end": v(58.98, 12) * mm});
            skLineSegment(sketch, "E54.6.0.38", {"start": v(59, 12) * mm, "end": v(59.03, 12) * mm});
            skLineSegment(sketch, "E54.6.0.39", {"start": v(59, 20) * mm, "end": v(59.1, 20) * mm});
            skArc(sketch, "E54.6.0.40", {"start": v(59.1, 16.29) * mm, "mid": v(59.12, 16.22) * mm, "end": v(59.2, 16.19) * mm});
            skArc(sketch, "E54.6.0.41", {"start": v(58.91, 16.29) * mm, "mid": v(58.88, 16.22) * mm, "end": v(58.8, 16.19) * mm});
            skPoint(sketch, "E54.7.0.0", {"position": v(68, 20) * mm});
            skLineSegment(sketch, "E54.7.0.1", {"start": v(68.1, 16.29) * mm, "end": v(68.1, 20) * mm});
            skLineSegment(sketch, "E54.7.0.2", {"start": v(68, 7.54) * mm, "end": v(69.92, 7.54) * mm});
            skLineSegment(sketch, "E54.7.0.3", {"start": v(67.98, 16.09) * mm, "end": v(67.98, 12) * mm});
            skPoint(sketch, "E54.7.0.4", {"position": v(70.83, 7.54) * mm});
            skLineSegment(sketch, "E54.7.0.5", {"start": v(68.25, 7.14) * mm, "end": v(68.25, 4) * mm});
            skLineSegment(sketch, "E54.7.0.6", {"start": v(64.27, 15.1) * mm, "end": v(64.92, 8.04) * mm});
            skPoint(sketch, "E54.7.0.7", {"position": v(68, 7.54) * mm});
            skPoint(sketch, "E54.7.0.8", {"position": v(71, 7.14) * mm});
            skPoint(sketch, "E54.7.0.9", {"position": v(71.83, 16.19) * mm});
            skPoint(sketch, "E54.7.0.10", {"position": v(68, 12) * mm});
            skPoint(sketch, "E54.7.0.11", {"position": v(68, 4) * mm});
            skLineSegment(sketch, "E54.7.0.12", {"start": v(67.9, 16.29) * mm, "end": v(67.9, 20) * mm});
            skLineSegment(sketch, "E54.7.0.13", {"start": v(67.75, 7.14) * mm, "end": v(67.75, 4) * mm});
            skPoint(sketch, "E54.7.0.14", {"position": v(71.62, 16.09) * mm});
            skLineSegment(sketch, "E54.7.0.15", {"start": v(68.03, 16.09) * mm, "end": v(68.03, 12) * mm});
            skLineSegment(sketch, "E54.7.0.16", {"start": v(64.48, 15) * mm, "end": v(65.08, 8.44) * mm});
            skLineSegment(sketch, "E54.7.0.17", {"start": v(67.81, 16.19) * mm, "end": v(65.27, 16.19) * mm});
            skLineSegment(sketch, "E54.7.0.18", {"start": v(71.73, 15.1) * mm, "end": v(71.08, 8.04) * mm});
            skArc(sketch, "E54.7.0.19", {"start": v(64.27, 15.1) * mm, "mid": v(64.53, 15.86) * mm, "end": v(65.27, 16.19) * mm});
            skLineSegment(sketch, "E54.7.0.20", {"start": v(71.52, 15) * mm, "end": v(70.92, 8.44) * mm});
            skArc(sketch, "E54.7.0.21", {"start": v(71.73, 15.1) * mm, "mid": v(71.47, 15.86) * mm, "end": v(70.73, 16.19) * mm});
            skLineSegment(sketch, "E54.7.0.22", {"start": v(68.19, 16.19) * mm, "end": v(70.73, 16.19) * mm});
            skLineSegment(sketch, "E54.7.0.23", {"start": v(67.98, 16.09) * mm, "end": v(65.48, 16.09) * mm});
            skLineSegment(sketch, "E54.7.0.24", {"start": v(68.25, 7.14) * mm, "end": v(70.09, 7.14) * mm});
            skArc(sketch, "E54.7.0.25", {"start": v(66.08, 7.54) * mm, "mid": v(65.4, 7.8) * mm, "end": v(65.08, 8.44) * mm});
            skArc(sketch, "E54.7.0.26", {"start": v(70.09, 7.14) * mm, "mid": v(70.76, 7.4) * mm, "end": v(71.08, 8.04) * mm});
            skArc(sketch, "E54.7.0.27", {"start": v(64.48, 15) * mm, "mid": v(64.74, 15.76) * mm, "end": v(65.48, 16.09) * mm});
            skLineSegment(sketch, "E54.7.0.28", {"start": v(68, 7.54) * mm, "end": v(66.08, 7.54) * mm});
            skArc(sketch, "E54.7.0.29", {"start": v(71.52, 15) * mm, "mid": v(71.26, 15.76) * mm, "end": v(70.52, 16.09) * mm});
            skArc(sketch, "E54.7.0.30", {"start": v(69.92, 7.54) * mm, "mid": v(70.6, 7.8) * mm, "end": v(70.92, 8.44) * mm});
            skLineSegment(sketch, "E54.7.0.31", {"start": v(68.03, 16.09) * mm, "end": v(70.52, 16.09) * mm});
            skArc(sketch, "E54.7.0.32", {"start": v(65.91, 7.14) * mm, "mid": v(65.24, 7.4) * mm, "end": v(64.92, 8.04) * mm});
            skLineSegment(sketch, "E54.7.0.33", {"start": v(67.75, 7.14) * mm, "end": v(65.91, 7.14) * mm});
            skLineSegment(sketch, "E54.7.0.34", {"start": v(68, 4) * mm, "end": v(67.75, 4) * mm});
            skLineSegment(sketch, "E54.7.0.35", {"start": v(68, 20) * mm, "end": v(67.91, 20) * mm});
            skLineSegment(sketch, "E54.7.0.36", {"start": v(68, 4) * mm, "end": v(68.25, 4) * mm});
            skLineSegment(sketch, "E54.7.0.37", {"start": v(68, 12) * mm, "end": v(67.98, 12) * mm});
            skLineSegment(sketch, "E54.7.0.38", {"start": v(68, 12) * mm, "end": v(68.03, 12) * mm});
            skLineSegment(sketch, "E54.7.0.39", {"start": v(68, 20) * mm, "end": v(68.1, 20) * mm});
            skArc(sketch, "E54.7.0.40", {"start": v(68.1, 16.29) * mm, "mid": v(68.12, 16.22) * mm, "end": v(68.2, 16.19) * mm});
            skArc(sketch, "E54.7.0.41", {"start": v(67.9, 16.29) * mm, "mid": v(67.88, 16.22) * mm, "end": v(67.8, 16.19) * mm});
            skLineSegment(sketch, "E54.direction1", {"start": v(4.75, 4) * mm, "end": v(13.75, 4) * mm, "construction": true});
            skSolve(sketch);
        }
        {
            var Q0;
            Q0 = qSketchRegion(id + "F13", true);
            extrude(context, id + "F14", {"entities" : qUnion([Q0]), "operationType" : NewBodyOperationType.REMOVE, "depth" : 0.12 * mm, "offsetDistance" : 25 * mm});
        }
    });
